# Revit family: Hager-Volta-IP30-sistema-CH-it
name_source: partatom
category: Electrical Equipment
units: mm (PartAtom-declared; Revit-internal decimal feet)

## family parameters
Cut with Voids When Loaded = No
Host = Face
Panel Configuration = Two Columns, Circuits Across
Part Type = Panelboard
Room Calculation Point = No
Round Connector Dimension = Use Diameter
Shared = No

## types (4) — shared parameters
EF000003 - Tipo di montaggio = EV000384 - A parete
EF000008 - Larghezza = 305 mm  [stored 1.00066 ft]
EF000049 - profondità = 97 mm  [stored 0.318241 ft]
EF000118 - con piastra di montaggio = No
EF001062 - esecuzione EMC = No
EF001088 - possibilità di applicazione = No
EF001134 - barra DIN = No
EF001596 - Attacco Lampada = EV000139 - plastica
EF002950 - Numero moduli DIN = 12
EF004462 - tipo di chiusura = EV000154 - altri
EF005474 - grado di protezione (IP) = EV006410 - IP30
EF006244 - coperchio/porta trasparente = Yes
EF006306 - con serratura = No
EF015776 - Morsettiera di terra = No
EF015777 - Morsettiera neutra = No
EF015941 - Segnale di passaggio porta = No
HG000001 - Numero di colonne = 1
HG000002 - Con porta = Yes
HG000003 - Gamma = Volta
HG000005 - Spessore = 3 mm  [stored 0.00984252 ft]
HG000006 - Ad incasso = No
HG000009 - Porta doppia a battente = No
HG000010 - Porte asimmetriche = No
HG000011 - File vuote nella parte basse = No
HG000017 - Distanza tra i poli = 18 mm  [stored 0.0590551 ft]
Manufacturer = Hager
Type Comments = Volta
zero-valued in all types: Default Elevation, EF000218 - profondità di incasso, EF000332 - Altezza della parte incassata, EF000846 - larghezza di montaggio, EF001131 - profondità interna, HG000007 - Numero di colonne vuote, HG000008 - Numero di file vuote

## per-type parameters (varying)
| type | EF000040 - Altezza | EF000116 - numero RAL | EF000266 - numero di file | HG000004 - Codice produttore | Model |
| A parete IP30 L305 A245 P97 12 Unità di divisione - G44037035 | 245 mm | 7035 | 1 | G44037035 | G44037035 |
| A parete IP30 L305 A245 P97 12 Unità di divisione - G44039010 | 245 mm | 9010 | 1 | G44039010 | G44039010 |
| A parete IP30 L305 A370 P97 12 Unità di divisione - G44047035 | 370 mm  [stored 1.21391 ft] | 7035 | 2 | G44047035 | G44047035 |
| A parete IP30 L305 A370 P97 12 Unità di divisione - G44049010 | 370 mm  [stored 1.21391 ft] | 9010 | 2 | G44049010 | G44049010 |

note: [stored X ft] marks values corroborated as IEEE doubles in the binary element streams (Revit-internal decimal feet)

## geometry (parser evidence)
native form markers: Sweep x17
no freeform markers — native parametric forms only
